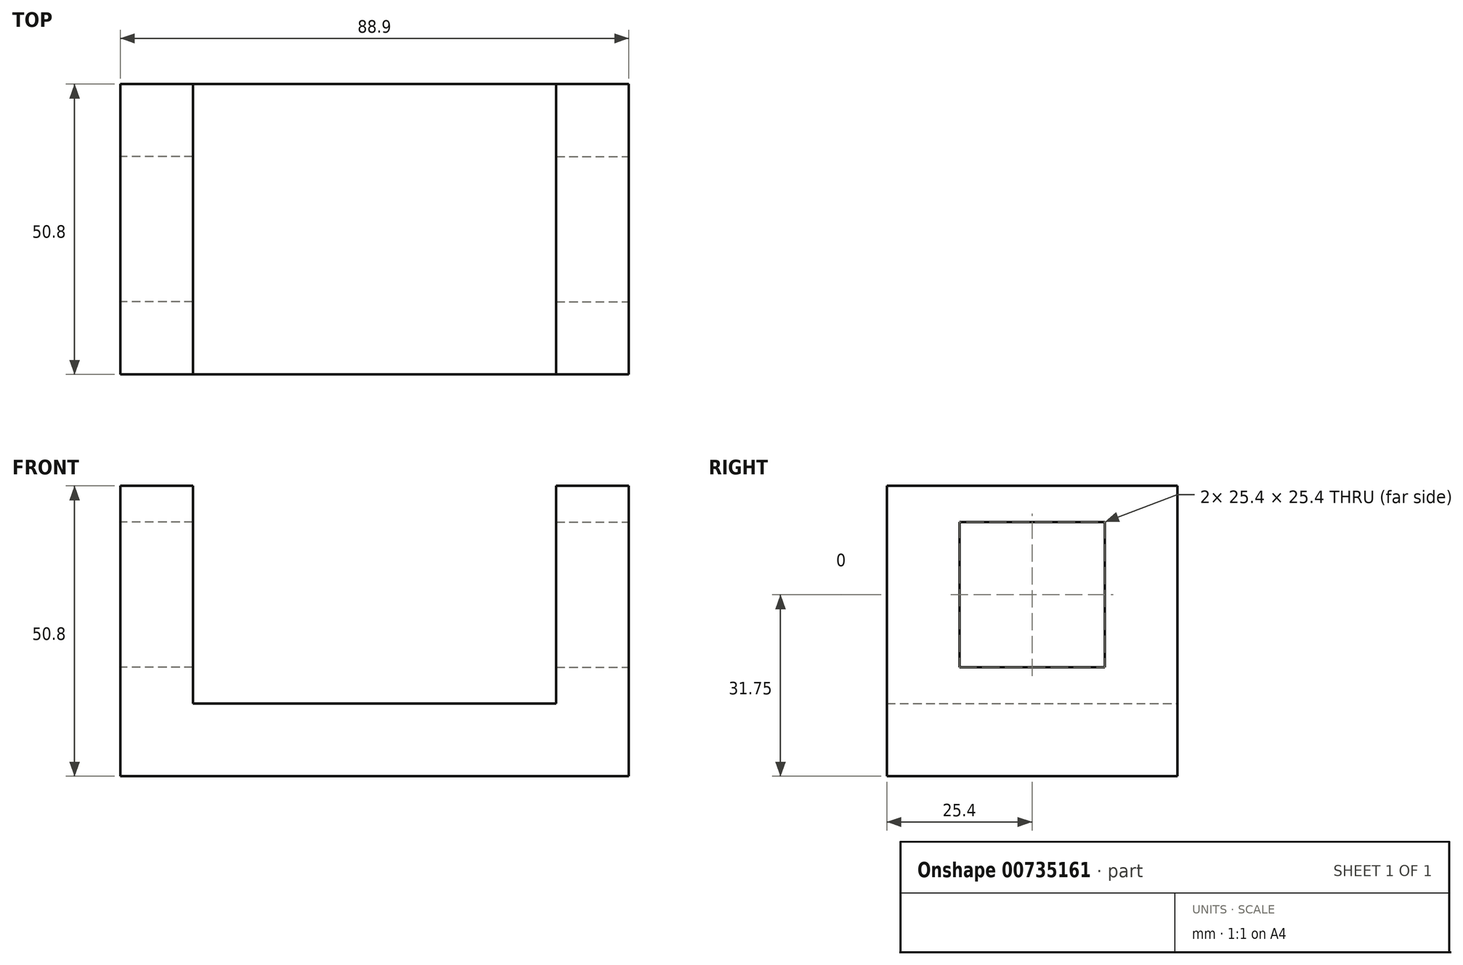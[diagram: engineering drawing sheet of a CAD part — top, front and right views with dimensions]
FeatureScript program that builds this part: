
annotation { "Feature Type Name" : "Feature", "Feature Type Description" : "" }
export const myFeature = defineFeature(function(context is Context, id is Id, definition is map)
    precondition{}
    {
        {
            var Q0;
            Q0=qCreatedBy(makeId("Front.planeOp"),FACE);
            var sketch = newSketch(context, id + "F0", { "sketchPlane" : qUnion([Q0])});
            skLineSegment(sketch, "E0", {"start": v(-51.66, 38.1) * mm, "end": v(-51.66, -12.7) * mm});
            skLineSegment(sketch, "E1", {"start": v(37.24, 38.1) * mm, "end": v(37.24, -12.7) * mm});
            skLineSegment(sketch, "E2", {"start": v(-51.66, -12.7) * mm, "end": v(37.24, -12.7) * mm});
            skLineSegment(sketch, "E3", {"start": v(-51.66, 38.1) * mm, "end": v(-38.96, 38.1) * mm});
            skLineSegment(sketch, "E4", {"start": v(37.24, 38.1) * mm, "end": v(24.54, 38.1) * mm});
            skLineSegment(sketch, "E5", {"start": v(-38.96, 38.1) * mm, "end": v(-38.96, 0) * mm});
            skLineSegment(sketch, "E6", {"start": v(24.54, 38.1) * mm, "end": v(24.54, 0) * mm});
            skLineSegment(sketch, "E7", {"start": v(-38.96, 0) * mm, "end": v(24.54, 0) * mm});
            skSolve(sketch);
        }
        {
            var Q0;
            Q0 = qSketchRegion(id + "F0", true);
            extrude(context, id + "F1", {"entities" : qUnion([Q0]), "depth" : 50.8 * mm, "offsetDistance" : 25.4 * mm});
        }
        {
            var Q0;
            Q0=makeQuery(id+"F1.opExtrude","SWEPT_FACE",FACE,{"disambiguationData":[OSD([sQuery(id+"F0.wireOp",EDGE,"E1")])]});
            var sketch = newSketch(context, id + "F2", { "sketchPlane" : qUnion([Q0])});
            skSolve(sketch);
        }
        {
            var Q0;
            {var subQ0=sQuery(id+"F0.wireOp",EDGE,"E1");Q0=makeQuery(id+"F2.imprint","IMPRINT",FACE,{"disambiguationData":[TD([[makeQuery(id+"F2.imprint","IMPRINT",EDGE,{"derivedFrom":makeQuery(id+"F1.opExtrude","CAP_EDGE",EDGE,{"disambiguationData":[OSD([subQ0])],"isStart":true})}),-1.0]])]});}
            var sketch = newSketch(context, id + "F3", { "sketchPlane" : qUnion([Q0])});
            skLineSegment(sketch, "E8.bottom", {"start": v(-38.1, 31.75) * mm, "end": v(-12.7, 31.75) * mm});
            skLineSegment(sketch, "E8.top", {"start": v(-38.1, 6.35) * mm, "end": v(-12.7, 6.35) * mm});
            skLineSegment(sketch, "E8.left", {"start": v(-38.1, 31.75) * mm, "end": v(-38.1, 6.35) * mm});
            skLineSegment(sketch, "E8.right", {"start": v(-12.7, 31.75) * mm, "end": v(-12.7, 6.35) * mm});
            skSolve(sketch);
        }
        {
            var Q0;
            Q0 = qSketchRegion(id + "F3", true);
            extrude(context, id + "F4", {"entities" : qUnion([Q0]), "operationType" : NewBodyOperationType.REMOVE, "oppositeDirection" : true, "depth" : 25.4 * mm, "offsetDistance" : 25.4 * mm});
        }
        {
            var Q0;
            Q0=makeQuery(id+"F1.opExtrude","SWEPT_FACE",FACE,{"disambiguationData":[OSD([sQuery(id+"F0.wireOp",EDGE,"E0")])]});
            var sketch = newSketch(context, id + "F5", { "sketchPlane" : qUnion([Q0])});
            skLineSegment(sketch, "E9.bottom", {"start": v(12.7, 31.75) * mm, "end": v(38.1, 31.75) * mm});
            skLineSegment(sketch, "E9.top", {"start": v(12.7, 6.35) * mm, "end": v(38.1, 6.35) * mm});
            skLineSegment(sketch, "E9.left", {"start": v(12.7, 31.75) * mm, "end": v(12.7, 6.35) * mm});
            skLineSegment(sketch, "E9.right", {"start": v(38.1, 31.75) * mm, "end": v(38.1, 6.35) * mm});
            skSolve(sketch);
        }
        {
            var Q0;
            Q0 = qSketchRegion(id + "F5", true);
            extrude(context, id + "F6", {"entities" : qUnion([Q0]), "operationType" : NewBodyOperationType.REMOVE, "oppositeDirection" : true, "depth" : 25.4 * mm, "offsetDistance" : 25.4 * mm});
        }
    });
